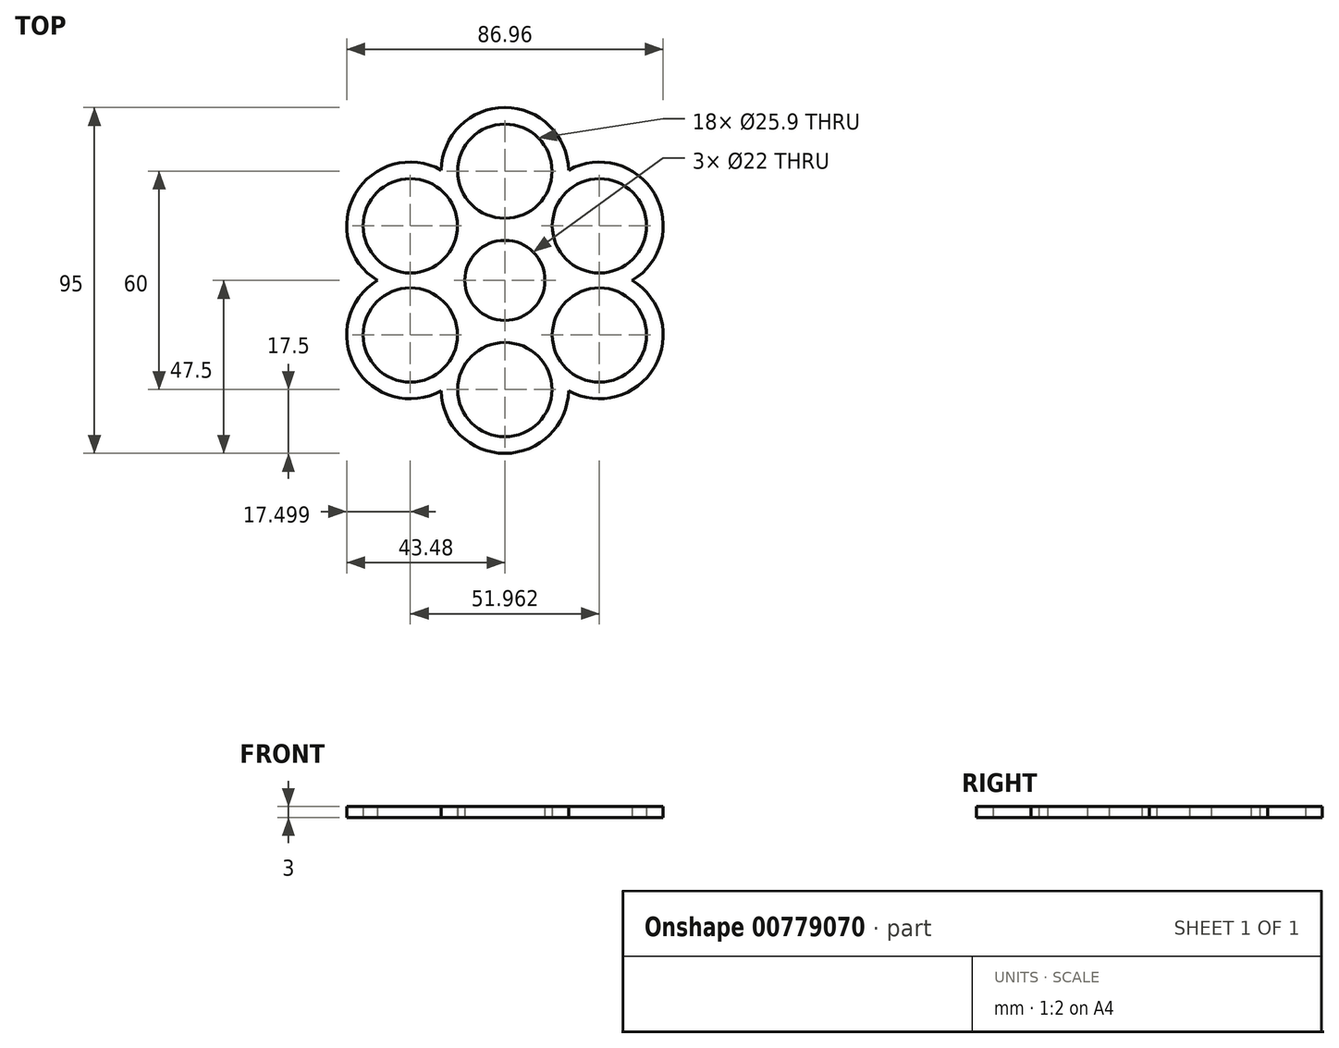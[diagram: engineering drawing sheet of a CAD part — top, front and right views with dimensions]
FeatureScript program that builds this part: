
annotation { "Feature Type Name" : "Feature", "Feature Type Description" : "" }
export const myFeature = defineFeature(function(context is Context, id is Id, definition is map)
    precondition{}
    {
        {
            var Q0;
            Q0=qCreatedBy(makeId("Top.planeOp"),FACE);
            var sketch = newSketch(context, id + "F0", { "sketchPlane" : qUnion([Q0])});
            skArc(sketch, "E0", {"start": v(5.5, 9.53) * mm, "mid": v(0, 11) * mm, "end": v(-5.5, 9.53) * mm});
            skCircle(sketch, "E1", {"center": v(0, 30) * mm, "radius": 12.95 * mm});
            skArc(sketch, "E2", {"start": v(17.5, 30.3) * mm, "mid": v(0, 47.5) * mm, "end": v(-17.5, 30.3) * mm});
            skArc(sketch, "E3.1.0", {"start": v(-17.5, 30.3) * mm, "mid": v(-41.14, 23.75) * mm, "end": v(-35, 0) * mm});
            skCircle(sketch, "E3.1.1", {"center": v(-25.98, 15) * mm, "radius": 12.95 * mm});
            skArc(sketch, "E3.1.3", {"start": v(-5.5, 9.53) * mm, "mid": v(-9.53, 5.5) * mm, "end": v(-11, 0) * mm});
            skArc(sketch, "E3.2.0", {"start": v(-35, 0) * mm, "mid": v(-41.14, -23.75) * mm, "end": v(-17.5, -30.3) * mm});
            skCircle(sketch, "E3.2.1", {"center": v(-25.98, -15) * mm, "radius": 12.95 * mm});
            skArc(sketch, "E3.2.3", {"start": v(-11, 0) * mm, "mid": v(-9.53, -5.5) * mm, "end": v(-5.5, -9.53) * mm});
            skArc(sketch, "E3.3.0", {"start": v(-17.5, -30.3) * mm, "mid": v(0, -47.5) * mm, "end": v(17.5, -30.3) * mm});
            skCircle(sketch, "E3.3.1", {"center": v(0, -30) * mm, "radius": 12.95 * mm});
            skArc(sketch, "E3.3.3", {"start": v(-5.5, -9.53) * mm, "mid": v(0, -11) * mm, "end": v(5.5, -9.53) * mm});
            skArc(sketch, "E3.4.0", {"start": v(17.5, -30.3) * mm, "mid": v(41.14, -23.75) * mm, "end": v(35, 0) * mm});
            skCircle(sketch, "E3.4.1", {"center": v(25.98, -15) * mm, "radius": 12.95 * mm});
            skArc(sketch, "E3.4.3", {"start": v(5.5, -9.53) * mm, "mid": v(9.53, -5.5) * mm, "end": v(11, 0) * mm});
            skArc(sketch, "E3.5.0", {"start": v(35, 0) * mm, "mid": v(41.14, 23.75) * mm, "end": v(17.5, 30.3) * mm});
            skCircle(sketch, "E3.5.1", {"center": v(25.98, 15) * mm, "radius": 12.95 * mm});
            skArc(sketch, "E3.5.3", {"start": v(11, 0) * mm, "mid": v(9.53, 5.5) * mm, "end": v(5.5, 9.53) * mm});
            skSolve(sketch);
        }
        {
            var Q0;
            Q0 = qSketchRegion(id + "F0", true);
            extrude(context, id + "F1", {"entities" : qUnion([Q0]), "depth" : 3 * mm, "offsetDistance" : 25 * mm});
        }
    });
